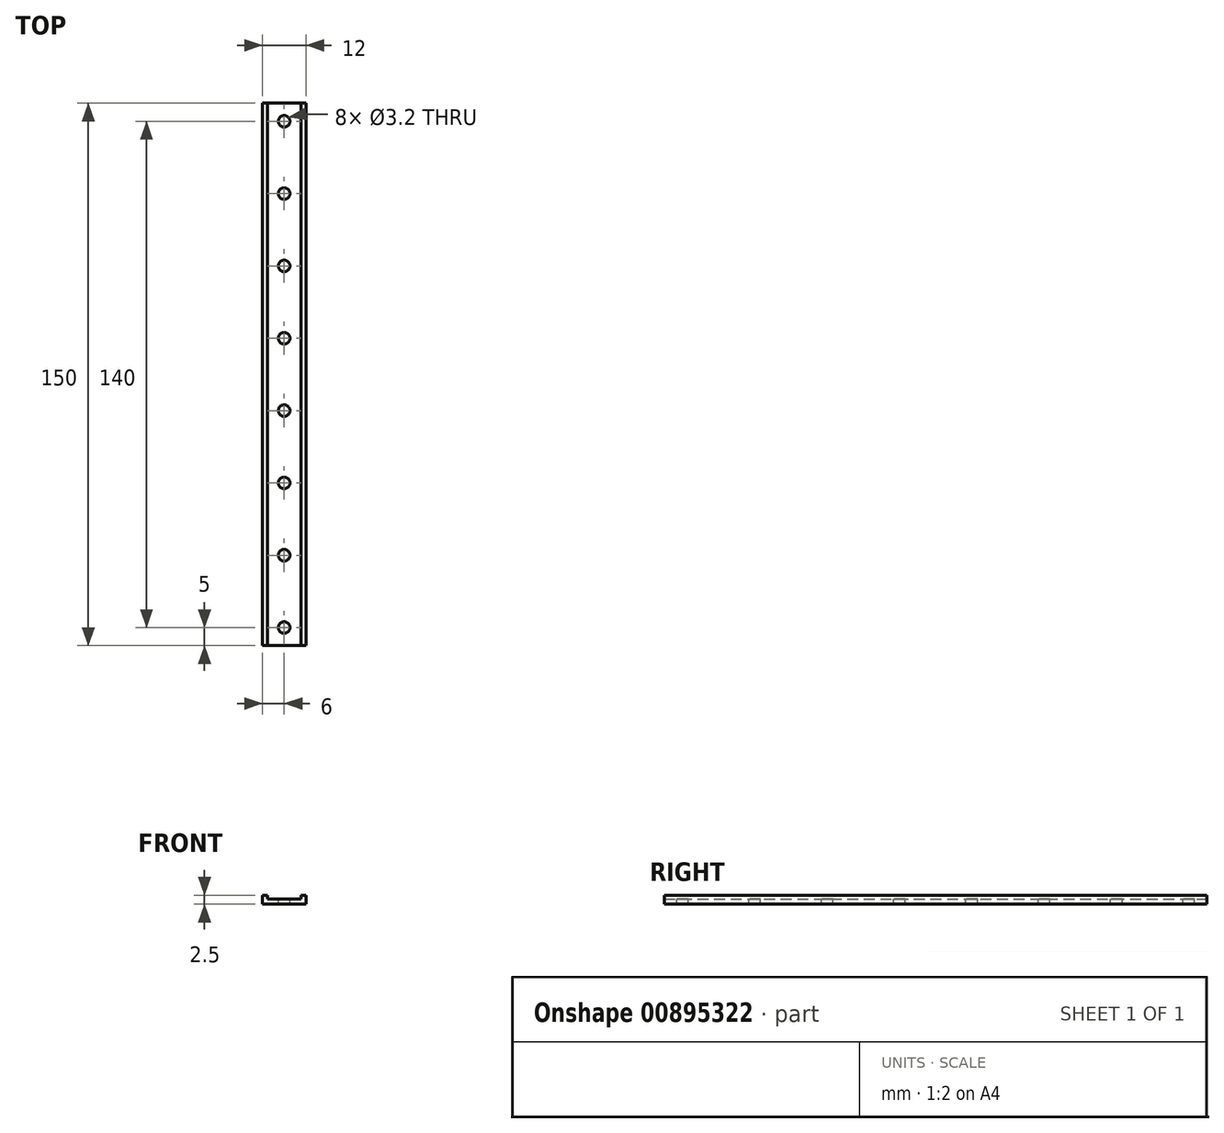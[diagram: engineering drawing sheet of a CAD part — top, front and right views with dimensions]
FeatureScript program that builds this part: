
annotation { "Feature Type Name" : "Feature", "Feature Type Description" : "" }
export const myFeature = defineFeature(function(context is Context, id is Id, definition is map)
    precondition{}
    {
        {
            var Q0;
            Q0=qCreatedBy(makeId("Front.planeOp"),FACE);
            var sketch = newSketch(context, id + "F0", { "sketchPlane" : qUnion([Q0])});
            skLineSegment(sketch, "E0", {"start": v(-6, 2.5) * mm, "end": v(-6, 0) * mm});
            skLineSegment(sketch, "E1", {"start": v(-6, 0) * mm, "end": v(6, 0) * mm});
            skLineSegment(sketch, "E2", {"start": v(6, 0) * mm, "end": v(6, 2.5) * mm});
            skLineSegment(sketch, "E3", {"start": v(6, 2.5) * mm, "end": v(4.6, 2.5) * mm});
            skLineSegment(sketch, "E4", {"start": v(4.6, 2.5) * mm, "end": v(4.6, 1.5) * mm});
            skLineSegment(sketch, "E5", {"start": v(4.6, 1.5) * mm, "end": v(-4.6, 1.5) * mm});
            skLineSegment(sketch, "E6", {"start": v(-4.6, 1.5) * mm, "end": v(-4.6, 2.5) * mm});
            skLineSegment(sketch, "E7", {"start": v(-4.6, 2.5) * mm, "end": v(-6, 2.5) * mm});
            skLineSegment(sketch, "E8", {"start": v(-5.62, 8) * mm, "end": v(5.47, 8) * mm, "construction": true});
            skSolve(sketch);
        }
        {
            var Q0;
            Q0 = qSketchRegion(id + "F0", true);
            extrude(context, id + "F1", {"entities" : qUnion([Q0]), "endBound" : BoundingType.SYMMETRIC, "depth" : 150 * mm, "offsetDistance" : 25 * mm});
        }
        {
            var Q0;
            Q0=makeQuery(id+"F1.opExtrude","SWEPT_FACE",FACE,{"disambiguationData":[OSD([sQuery(id+"F0.wireOp",EDGE,"E5")])]});
            var sketch = newSketch(context, id + "F2", { "sketchPlane" : qUnion([Q0])});
            skCircle(sketch, "E9", {"center": v(0, -70) * mm, "radius": 1.6 * mm});
            skCircle(sketch, "E10.0.1.0", {"center": v(0, -50) * mm, "radius": 1.6 * mm});
            skCircle(sketch, "E10.0.2.0", {"center": v(0, -30) * mm, "radius": 1.6 * mm});
            skCircle(sketch, "E10.0.3.0", {"center": v(0, -10) * mm, "radius": 1.6 * mm});
            skCircle(sketch, "E10.0.4.0", {"center": v(0, 10) * mm, "radius": 1.6 * mm});
            skCircle(sketch, "E10.0.5.0", {"center": v(0, 30) * mm, "radius": 1.6 * mm});
            skCircle(sketch, "E10.0.6.0", {"center": v(0, 50) * mm, "radius": 1.6 * mm});
            skCircle(sketch, "E10.0.7.0", {"center": v(0, 70) * mm, "radius": 1.6 * mm});
            skLineSegment(sketch, "E10.direction1", {"start": v(0, -70) * mm, "end": v(1, -70) * mm, "construction": true});
            skLineSegment(sketch, "E10.direction2", {"start": v(0, -70) * mm, "end": v(0, -50) * mm, "construction": true});
            skSolve(sketch);
        }
        {
            var Q0;
            Q0 = qSketchRegion(id + "F2", true);
            extrude(context, id + "F3", {"entities" : qUnion([Q0]), "operationType" : NewBodyOperationType.REMOVE, "endBound" : BoundingType.UP_TO_NEXT, "oppositeDirection" : true, "depth" : 25 * mm, "offsetDistance" : 25 * mm});
        }
    });
